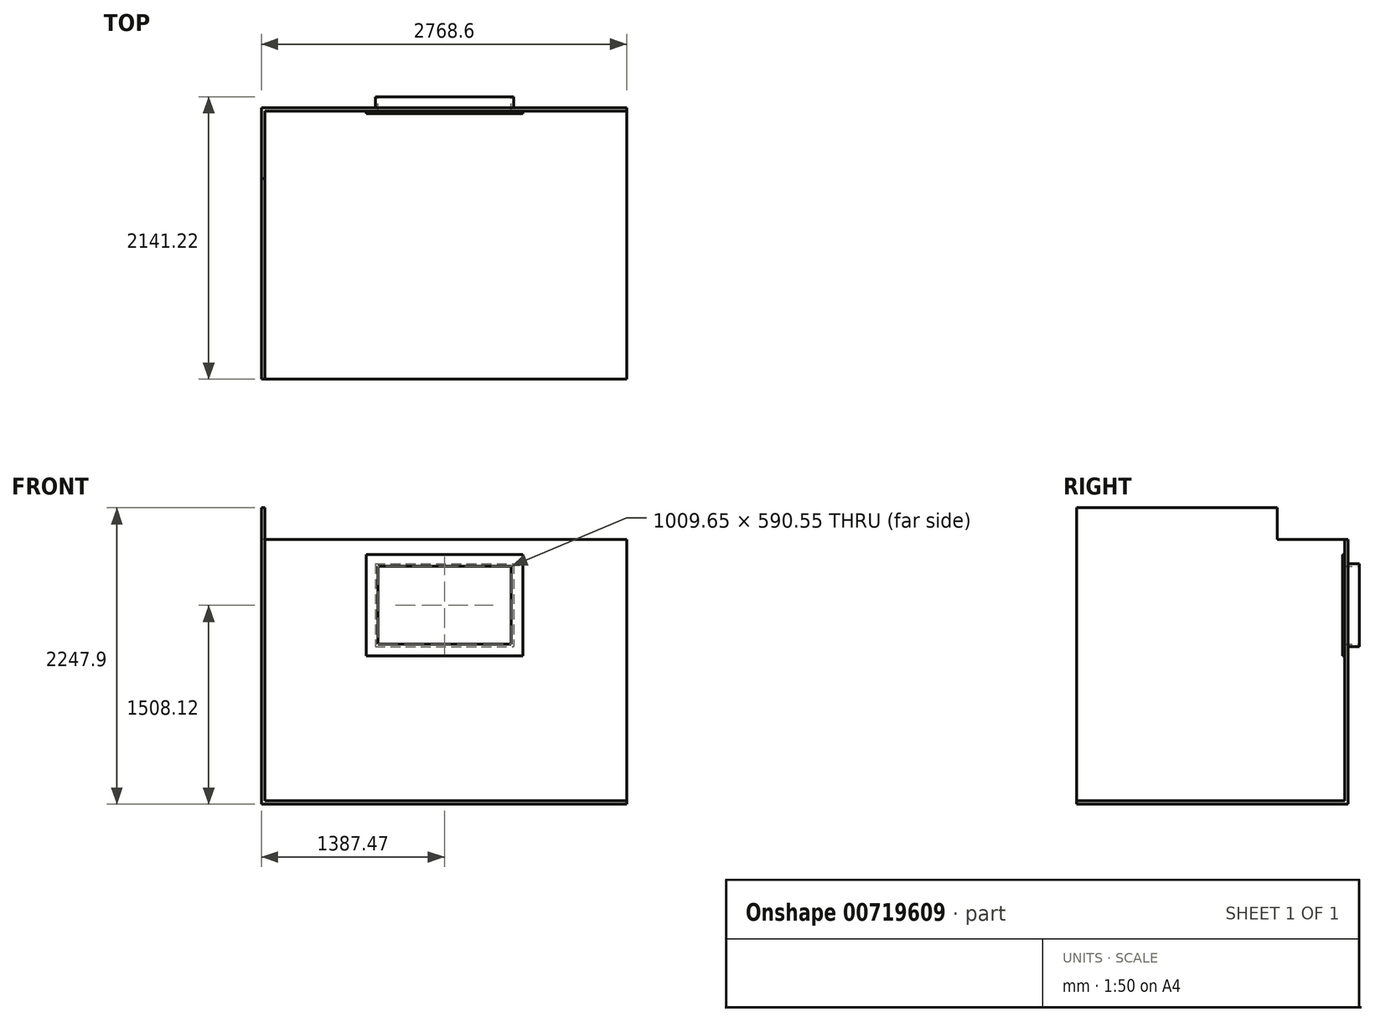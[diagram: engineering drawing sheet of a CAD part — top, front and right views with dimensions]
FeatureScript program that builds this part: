
annotation { "Feature Type Name" : "Feature", "Feature Type Description" : "" }
export const myFeature = defineFeature(function(context is Context, id is Id, definition is map)
    precondition{}
    {
        {
            var Q0;
            Q0=qCreatedBy(makeId("Top.planeOp"),FACE);
            var sketch = newSketch(context, id + "F0", { "sketchPlane" : qUnion([Q0])});
            skLineSegment(sketch, "E0", {"start": v(0, 0) * mm, "end": v(2743.2, 0) * mm});
            skLineSegment(sketch, "E1", {"start": v(0, 0) * mm, "end": v(0, -2032) * mm});
            skLineSegment(sketch, "E2", {"start": v(0, -2032) * mm, "end": v(2743.2, -2032) * mm});
            skLineSegment(sketch, "E3", {"start": v(2743.2, 0) * mm, "end": v(2743.2, -2032) * mm});
            skSolve(sketch);
        }
        {
            var Q0;
            Q0=makeQuery(id+"F0.imprint","IMPRINT",FACE,{"disambiguationData":[TD([[makeQuery(id+"F0.imprint","IMPRINT",EDGE,{"derivedFrom":sQuery(id+"F0.wireOp",EDGE,"E0")}),-1.0]])]});
            extrude(context, id + "F1", {"entities" : qUnion([Q0]), "depth" : 25.4 * mm, "offsetDistance" : 25.4 * mm});
        }
        {
            var Q0;
            Q0=qCreatedBy(makeId("Top.planeOp"),FACE);
            var sketch = newSketch(context, id + "F2", { "sketchPlane" : qUnion([Q0])});
            skLineSegment(sketch, "E4.bottom", {"start": v(0, 0) * mm, "end": v(-25.4, 0) * mm});
            skLineSegment(sketch, "E4.top", {"start": v(0, -2032) * mm, "end": v(-25.4, -2032) * mm});
            skLineSegment(sketch, "E4.left", {"start": v(0, 0) * mm, "end": v(0, -2032) * mm});
            skLineSegment(sketch, "E4.right", {"start": v(-25.4, 0) * mm, "end": v(-25.4, -2032) * mm});
            skLineSegment(sketch, "E5.bottom", {"start": v(-25.4, 0) * mm, "end": v(2743.2, 0) * mm});
            skLineSegment(sketch, "E5.top", {"start": v(-25.4, 25.4) * mm, "end": v(2743.2, 25.4) * mm});
            skLineSegment(sketch, "E5.left", {"start": v(-25.4, 0) * mm, "end": v(-25.4, 25.4) * mm});
            skLineSegment(sketch, "E5.right", {"start": v(2743.2, 0) * mm, "end": v(2743.2, 25.4) * mm});
            skSolve(sketch);
        }
        {
            var Q0;
            Q0=makeQuery(id+"F2.imprint","IMPRINT",FACE,{"disambiguationData":[TD([[makeQuery(id+"F2.imprint","IMPRINT",EDGE,{"derivedFrom":sQuery(id+"F2.wireOp",EDGE,"E4.top")}),-1.0]])]});
            var Q1;
            Q1=makeQuery(id+"F2.imprint","IMPRINT",FACE,{"disambiguationData":[TD([[makeQuery(id+"F2.imprint","IMPRINT",EDGE,{"derivedFrom":sQuery(id+"F2.wireOp",EDGE,"E5.top")}),-1.0]])]});
            extrude(context, id + "F3", {"entities" : qUnion([Q0, Q1]), "operationType" : NewBodyOperationType.ADD, "depth" : 2006.6 * mm, "offsetDistance" : 25.4 * mm});
        }
        {
            var Q0;
            Q0=makeQuery(id+"F3.opExtrude","SWEPT_FACE",FACE,{"disambiguationData":[OSD([sQuery(id+"F2.wireOp",EDGE,"E5.bottom")])]});
            var sketch = newSketch(context, id + "F4", { "sketchPlane" : qUnion([Q0])});
            skLineSegment(sketch, "E6.bottom", {"start": v(768.35, 1892.3) * mm, "end": v(1955.8, 1892.3) * mm});
            skLineSegment(sketch, "E6.top", {"start": v(768.35, 1123.95) * mm, "end": v(1955.8, 1123.95) * mm});
            skLineSegment(sketch, "E6.left", {"start": v(768.35, 1892.3) * mm, "end": v(768.35, 1123.95) * mm});
            skLineSegment(sketch, "E6.right", {"start": v(1955.8, 1892.3) * mm, "end": v(1955.8, 1123.95) * mm});
            skLineSegment(sketch, "E7.0", {"start": v(857.25, 1803.4) * mm, "end": v(857.25, 1212.85) * mm});
            skLineSegment(sketch, "E7.1", {"start": v(857.25, 1803.4) * mm, "end": v(1866.9, 1803.4) * mm});
            skLineSegment(sketch, "E7.2", {"start": v(1866.9, 1803.4) * mm, "end": v(1866.9, 1212.85) * mm});
            skLineSegment(sketch, "E7.3", {"start": v(857.25, 1212.85) * mm, "end": v(1866.9, 1212.85) * mm});
            skSolve(sketch);
        }
        {
            var Q0;
            Q0=makeQuery(id+"F4.imprint","IMPRINT",FACE,{"disambiguationData":[TD([[makeQuery(id+"F4.imprint","IMPRINT",EDGE,{"derivedFrom":sQuery(id+"F4.wireOp",EDGE,"E6.bottom")}),-1.0]])]});
            extrude(context, id + "F5", {"entities" : qUnion([Q0]), "operationType" : NewBodyOperationType.ADD, "depth" : 17.78 * mm, "offsetDistance" : 25.4 * mm});
        }
        {
            var Q0;
            Q0=makeQuery(id+"F5.boolean.opBoolean","SPLIT",FACE,{"disambiguationData":[TD([makeQuery(id+"F5.opExtrude","SWEPT_FACE",FACE,{"disambiguationData":[OSD([sQuery(id+"F4.wireOp",EDGE,"E7.0")])]})])],"derivedFrom":makeQuery(id+"F3.opExtrude","SWEPT_FACE",FACE,{"disambiguationData":[OSD([sQuery(id+"F2.wireOp",EDGE,"E5.bottom")])]})});
            extrude(context, id + "F6", {"entities" : qUnion([Q0]), "operationType" : NewBodyOperationType.REMOVE, "oppositeDirection" : true, "depth" : 25.4 * mm, "offsetDistance" : 25.4 * mm});
        }
        {
            var Q0;
            Q0=makeQuery(id+"F3.opExtrude","SWEPT_FACE",FACE,{"disambiguationData":[OSD([sQuery(id+"F2.wireOp",EDGE,"E5.top")])]});
            var sketch = newSketch(context, id + "F7", { "sketchPlane" : qUnion([Q0])});
            skLineSegment(sketch, "E8.0", {"start": v(-1885.95, 1822.45) * mm, "end": v(-1885.95, 1193.8) * mm});
            skLineSegment(sketch, "E8.1", {"start": v(-838.2, 1822.45) * mm, "end": v(-1885.95, 1822.45) * mm});
            skLineSegment(sketch, "E8.2", {"start": v(-838.2, 1822.45) * mm, "end": v(-838.2, 1193.8) * mm});
            skLineSegment(sketch, "E8.3", {"start": v(-838.2, 1193.8) * mm, "end": v(-1885.95, 1193.8) * mm});
            skSolve(sketch);
        }
        {
            var Q0;
            Q0=makeQuery(id+"F7.imprint","IMPRINT",FACE,{"disambiguationData":[TD([[makeQuery(id+"F7.imprint","IMPRINT",EDGE,{"derivedFrom":sQuery(id+"F7.wireOp",EDGE,"E8.0")}),1.0]])]});
            extrude(context, id + "F8", {"entities" : qUnion([Q0]), "operationType" : NewBodyOperationType.ADD, "depth" : 83.82 * mm, "offsetDistance" : 25.4 * mm});
        }
        {
            var Q0;
            Q0=makeQuery(id+"F3.opExtrude","CAP_FACE",FACE,{"disambiguationData":[OSD([sQuery(id+"F2.wireOp",EDGE,"E4.top"),sQuery(id+"F2.wireOp",EDGE,"E4.left"),sQuery(id+"F2.wireOp",EDGE,"E4.right"),sQuery(id+"F2.wireOp",EDGE,"E5.bottom"),sQuery(id+"F2.wireOp",EDGE,"E5.top"),sQuery(id+"F2.wireOp",EDGE,"E5.left"),sQuery(id+"F2.wireOp",EDGE,"E5.right")])],"isStart":false});
            var sketch = newSketch(context, id + "F9", { "sketchPlane" : qUnion([Q0])});
            skLineSegment(sketch, "E9", {"start": v(0, -511.18) * mm, "end": v(-25.4, -511.18) * mm});
            skLineSegment(sketch, "E10.0", {"start": v(-25.4, -511.18) * mm, "end": v(-25.4, -2032) * mm});
            skLineSegment(sketch, "E11.0", {"start": v(0, -511.18) * mm, "end": v(0, -2032) * mm});
            skLineSegment(sketch, "E12.0", {"start": v(0, -2032) * mm, "end": v(-25.4, -2032) * mm});
            skPoint(sketch, "E13.orphan", {"position": v(0, 0) * mm});
            skPoint(sketch, "E14.orphan", {"position": v(-25.4, 25.4) * mm});
            skSolve(sketch);
        }
        {
            var Q0;
            Q0 = qSketchRegion(id + "F9", true);
            extrude(context, id + "F10", {"entities" : qUnion([Q0]), "operationType" : NewBodyOperationType.ADD, "depth" : 241.3 * mm, "offsetDistance" : 25.4 * mm});
        }
    });
